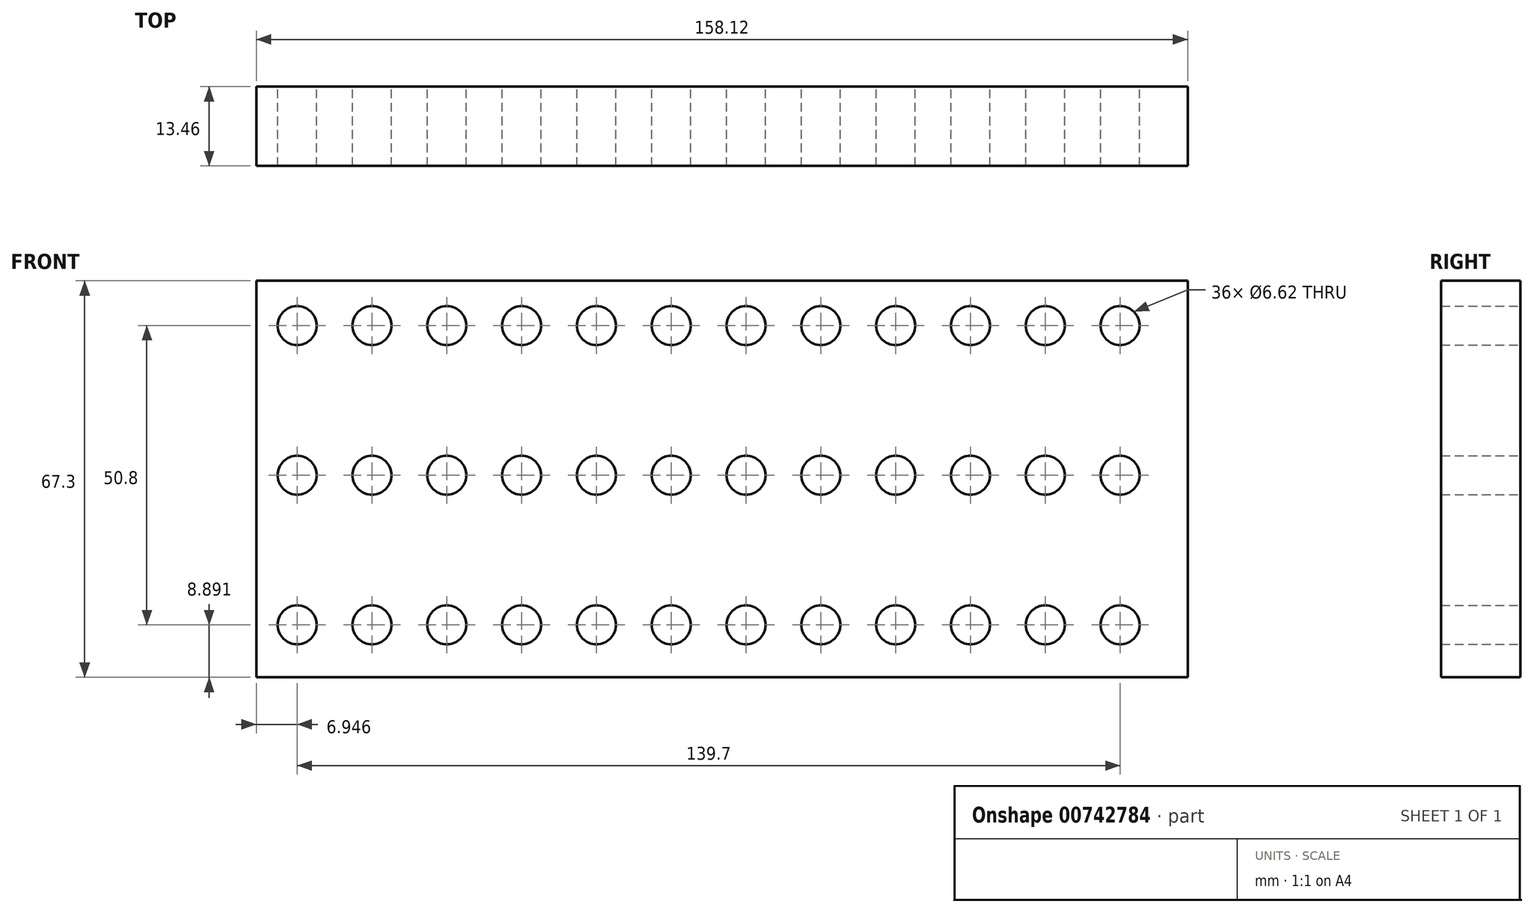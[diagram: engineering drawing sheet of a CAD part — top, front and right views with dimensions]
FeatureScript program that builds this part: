
annotation { "Feature Type Name" : "Feature", "Feature Type Description" : "" }
export const myFeature = defineFeature(function(context is Context, id is Id, definition is map)
    precondition{}
    {
        {
            var Q0;
            Q0=qCreatedBy(makeId("Front.planeOp"),FACE);
            var sketch = newSketch(context, id + "F0", { "sketchPlane" : qUnion([Q0])});
            skLineSegment(sketch, "E0.bottom", {"start": v(0, 0) * mm, "end": v(158.12, 0) * mm});
            skLineSegment(sketch, "E0.top", {"start": v(0, 67.3) * mm, "end": v(158.12, 67.3) * mm});
            skLineSegment(sketch, "E0.left", {"start": v(0, 0) * mm, "end": v(0, 67.3) * mm});
            skLineSegment(sketch, "E0.right", {"start": v(158.12, 0) * mm, "end": v(158.12, 67.3) * mm});
            skCircle(sketch, "E1", {"center": v(6.95, 59.7) * mm, "radius": 3.31 * mm});
            skCircle(sketch, "E2.0.1.0", {"center": v(6.95, 34.3) * mm, "radius": 3.31 * mm});
            skCircle(sketch, "E2.0.2.0", {"center": v(6.95, 8.9) * mm, "radius": 3.31 * mm});
            skCircle(sketch, "E2.1.0.0", {"center": v(19.65, 59.7) * mm, "radius": 3.31 * mm});
            skCircle(sketch, "E2.1.1.0", {"center": v(19.65, 34.3) * mm, "radius": 3.31 * mm});
            skCircle(sketch, "E2.1.2.0", {"center": v(19.65, 8.9) * mm, "radius": 3.31 * mm});
            skCircle(sketch, "E2.2.0.0", {"center": v(32.35, 59.7) * mm, "radius": 3.31 * mm});
            skCircle(sketch, "E2.2.1.0", {"center": v(32.35, 34.3) * mm, "radius": 3.31 * mm});
            skCircle(sketch, "E2.2.2.0", {"center": v(32.35, 8.9) * mm, "radius": 3.31 * mm});
            skCircle(sketch, "E2.3.0.0", {"center": v(45.05, 59.7) * mm, "radius": 3.31 * mm});
            skCircle(sketch, "E2.3.1.0", {"center": v(45.05, 34.3) * mm, "radius": 3.31 * mm});
            skCircle(sketch, "E2.3.2.0", {"center": v(45.05, 8.9) * mm, "radius": 3.31 * mm});
            skCircle(sketch, "E2.4.0.0", {"center": v(57.75, 59.7) * mm, "radius": 3.31 * mm});
            skCircle(sketch, "E2.4.1.0", {"center": v(57.75, 34.3) * mm, "radius": 3.31 * mm});
            skCircle(sketch, "E2.4.2.0", {"center": v(57.75, 8.9) * mm, "radius": 3.31 * mm});
            skCircle(sketch, "E2.5.0.0", {"center": v(70.45, 59.7) * mm, "radius": 3.31 * mm});
            skCircle(sketch, "E2.5.1.0", {"center": v(70.45, 34.3) * mm, "radius": 3.31 * mm});
            skCircle(sketch, "E2.5.2.0", {"center": v(70.45, 8.9) * mm, "radius": 3.31 * mm});
            skCircle(sketch, "E2.6.0.0", {"center": v(83.15, 59.7) * mm, "radius": 3.31 * mm});
            skCircle(sketch, "E2.6.1.0", {"center": v(83.15, 34.3) * mm, "radius": 3.31 * mm});
            skCircle(sketch, "E2.6.2.0", {"center": v(83.15, 8.9) * mm, "radius": 3.31 * mm});
            skCircle(sketch, "E2.7.0.0", {"center": v(95.85, 59.7) * mm, "radius": 3.31 * mm});
            skCircle(sketch, "E2.7.1.0", {"center": v(95.85, 34.3) * mm, "radius": 3.31 * mm});
            skCircle(sketch, "E2.7.2.0", {"center": v(95.85, 8.9) * mm, "radius": 3.31 * mm});
            skCircle(sketch, "E2.8.0.0", {"center": v(108.55, 59.7) * mm, "radius": 3.31 * mm});
            skCircle(sketch, "E2.8.1.0", {"center": v(108.55, 34.3) * mm, "radius": 3.31 * mm});
            skCircle(sketch, "E2.8.2.0", {"center": v(108.55, 8.9) * mm, "radius": 3.31 * mm});
            skLineSegment(sketch, "E2.direction1", {"start": v(6.95, 59.7) * mm, "end": v(19.65, 59.7) * mm, "construction": true});
            skLineSegment(sketch, "E2.direction2", {"start": v(6.95, 59.7) * mm, "end": v(6.95, 34.3) * mm, "construction": true});
            skCircle(sketch, "E3.0.9.0", {"center": v(121.25, 59.7) * mm, "radius": 3.31 * mm});
            skCircle(sketch, "E3.0.9.1", {"center": v(121.25, 34.3) * mm, "radius": 3.31 * mm});
            skCircle(sketch, "E3.0.9.2", {"center": v(121.25, 8.9) * mm, "radius": 3.31 * mm});
            skCircle(sketch, "E3.0.10.0", {"center": v(133.95, 59.7) * mm, "radius": 3.31 * mm});
            skCircle(sketch, "E3.0.10.1", {"center": v(133.95, 34.3) * mm, "radius": 3.31 * mm});
            skCircle(sketch, "E3.0.10.2", {"center": v(133.95, 8.9) * mm, "radius": 3.31 * mm});
            skCircle(sketch, "E3.0.11.0", {"center": v(146.65, 59.7) * mm, "radius": 3.31 * mm});
            skCircle(sketch, "E3.0.11.1", {"center": v(146.65, 34.3) * mm, "radius": 3.31 * mm});
            skCircle(sketch, "E3.0.11.2", {"center": v(146.65, 8.9) * mm, "radius": 3.31 * mm});
            skSolve(sketch);
        }
        {
            var Q0;
            Q0=makeQuery(id+"F0.imprint","IMPRINT",FACE,{"disambiguationData":[TD([[makeQuery(id+"F0.imprint","IMPRINT",EDGE,{"derivedFrom":sQuery(id+"F0.wireOp",EDGE,"E0.bottom")}),1.0]])]});
            extrude(context, id + "F1", {"entities" : qUnion([Q0]), "depth" : 13.46 * mm, "offsetDistance" : 25.4 * mm});
        }
    });
